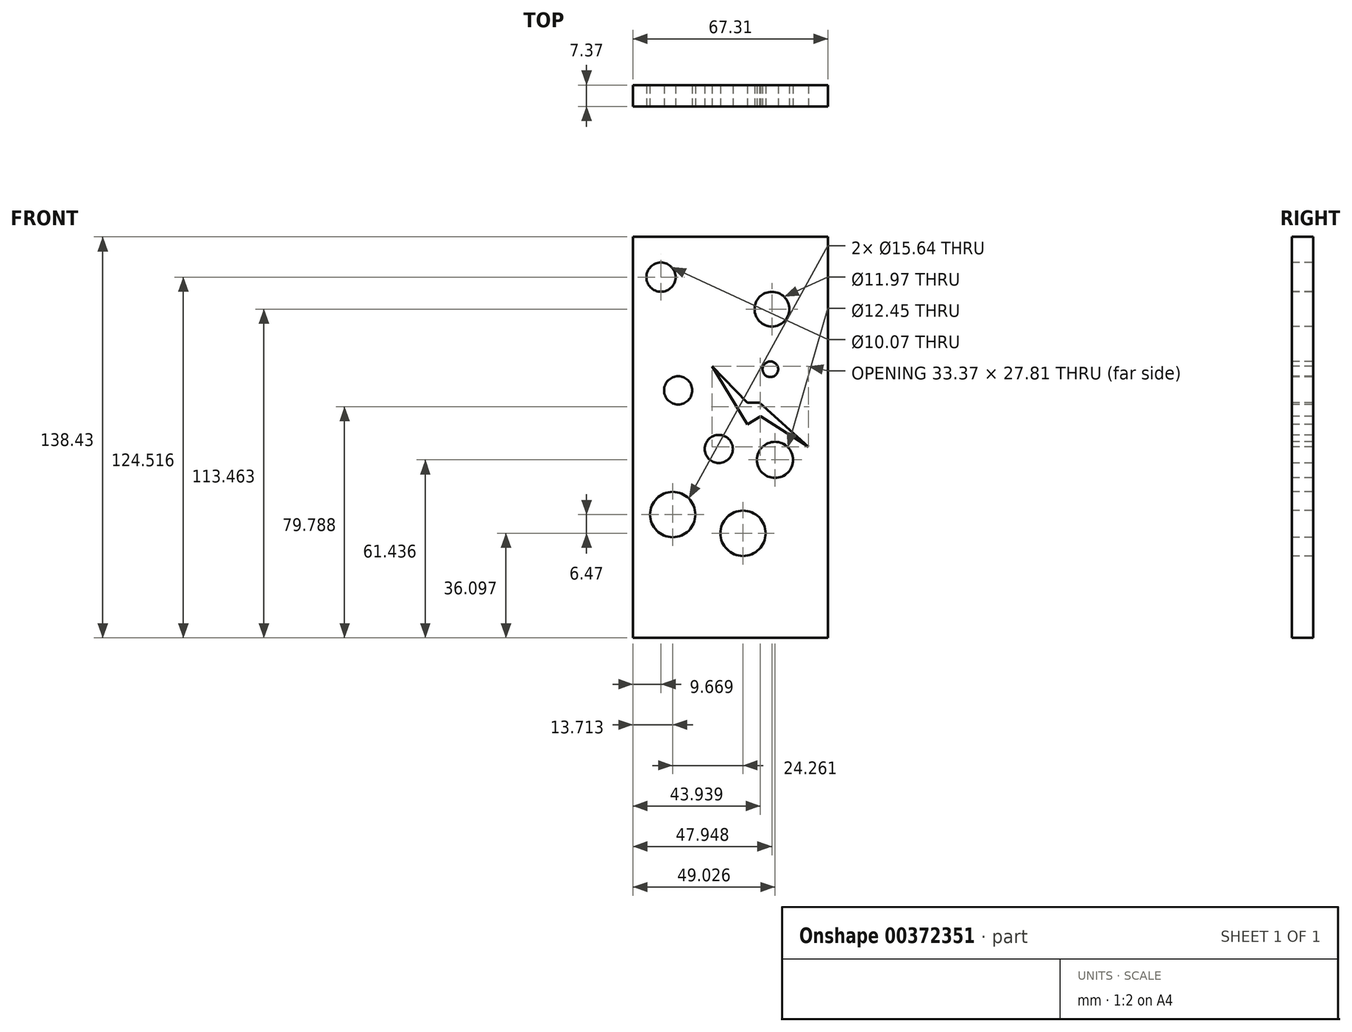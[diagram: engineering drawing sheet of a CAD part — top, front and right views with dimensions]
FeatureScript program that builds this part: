
annotation { "Feature Type Name" : "Feature", "Feature Type Description" : "" }
export const myFeature = defineFeature(function(context is Context, id is Id, definition is map)
    precondition{}
    {
        {
            var Q0;
            Q0=qCreatedBy(makeId("Front.planeOp"),FACE);
            var sketch = newSketch(context, id + "F0", { "sketchPlane" : qUnion([Q0])});
            skLineSegment(sketch, "E0.bottom", {"start": v(-21.53, 89.9) * mm, "end": v(45.78, 89.9) * mm});
            skLineSegment(sketch, "E0.top", {"start": v(-21.53, -48.52) * mm, "end": v(45.78, -48.52) * mm});
            skLineSegment(sketch, "E0.left", {"start": v(-21.53, 89.9) * mm, "end": v(-21.53, -48.52) * mm});
            skLineSegment(sketch, "E0.right", {"start": v(45.78, 89.9) * mm, "end": v(45.78, -48.52) * mm});
            skSolve(sketch);
        }
        {
            var Q0;
            Q0 = qSketchRegion(id + "F0", true);
            extrude(context, id + "F1", {"entities" : qUnion([Q0]), "depth" : 7.37 * mm});
        }
        {
            var Q0;
            Q0=makeQuery(id+"F1.opExtrude","CAP_FACE",FACE,{"disambiguationData":[OSD([sQuery(id+"F0.wireOp",EDGE,"E0.bottom"),sQuery(id+"F0.wireOp",EDGE,"E0.top"),sQuery(id+"F0.wireOp",EDGE,"E0.left"),sQuery(id+"F0.wireOp",EDGE,"E0.right")])],"isStart":false});
            var sketch = newSketch(context, id + "F2", { "sketchPlane" : qUnion([Q0])});
            skCircle(sketch, "E1", {"center": v(-11.86, 76) * mm, "radius": 5.04 * mm});
            skCircle(sketch, "E2", {"center": v(-5.93, 36.9) * mm, "radius": 4.86 * mm});
            skCircle(sketch, "E3", {"center": v(8.09, 16.7) * mm, "radius": 4.85 * mm});
            skCircle(sketch, "E4", {"center": v(27.5, 12.92) * mm, "radius": 6.22 * mm});
            skCircle(sketch, "E5", {"center": v(-7.82, -5.95) * mm, "radius": 7.82 * mm});
            skCircle(sketch, "E6", {"center": v(16.44, -12.42) * mm, "radius": 7.82 * mm});
            skCircle(sketch, "E7", {"center": v(25.88, 44.19) * mm, "radius": 2.7 * mm});
            skCircle(sketch, "E8", {"center": v(26.42, 64.94) * mm, "radius": 5.99 * mm});
            skSolve(sketch);
        }
        {
            var Q0;
            Q0=makeQuery(id+"F2.imprint","IMPRINT",FACE,{"disambiguationData":[TD([[makeQuery(id+"F2.imprint","IMPRINT",EDGE,{"derivedFrom":sQuery(id+"F2.wireOp",EDGE,"E8")}),1.0]])]});
            var Q1;
            Q1 = qSketchRegion(id + "F2", true);
            extrude(context, id + "F3", {"entities" : qUnion([Q0, Q1]), "operationType" : NewBodyOperationType.REMOVE, "oppositeDirection" : true, "depth" : 25.4 * mm});
        }
        {
            var Q0;
            Q0=makeQuery(id+"F1.opExtrude","CAP_FACE",FACE,{"disambiguationData":[OSD([sQuery(id+"F0.wireOp",EDGE,"E0.bottom"),sQuery(id+"F0.wireOp",EDGE,"E0.top"),sQuery(id+"F0.wireOp",EDGE,"E0.left"),sQuery(id+"F0.wireOp",EDGE,"E0.right")])],"isStart":false});
            var sketch = newSketch(context, id + "F4", { "sketchPlane" : qUnion([Q0])});
            skLineSegment(sketch, "E9", {"start": v(5.73, 45.17) * mm, "end": v(17.94, 25.15) * mm});
            skLineSegment(sketch, "E10", {"start": v(17.94, 25.15) * mm, "end": v(22.55, 27.97) * mm});
            skLineSegment(sketch, "E11", {"start": v(22.55, 27.97) * mm, "end": v(39.1, 17.36) * mm});
            skLineSegment(sketch, "E12", {"start": v(39.1, 17.36) * mm, "end": v(22.15, 32.63) * mm});
            skLineSegment(sketch, "E13", {"start": v(22.15, 32.63) * mm, "end": v(17.94, 32.63) * mm});
            skLineSegment(sketch, "E14", {"start": v(17.94, 32.63) * mm, "end": v(5.73, 45.17) * mm});
            skLineSegment(sketch, "E15", {"start": v(0, -26.8) * mm, "end": v(34.04, -26.8) * mm});
            skSolve(sketch);
        }
        {
            var Q0;
            Q0=makeQuery(id+"F4.imprint","IMPRINT",FACE,{"disambiguationData":[TD([[makeQuery(id+"F4.imprint","IMPRINT",EDGE,{"derivedFrom":sQuery(id+"F4.wireOp",EDGE,"E9")}),1.0]])]});
            extrude(context, id + "F5", {"entities" : qUnion([Q0]), "operationType" : NewBodyOperationType.REMOVE, "oppositeDirection" : true, "depth" : 25.4 * mm});
        }
    });
